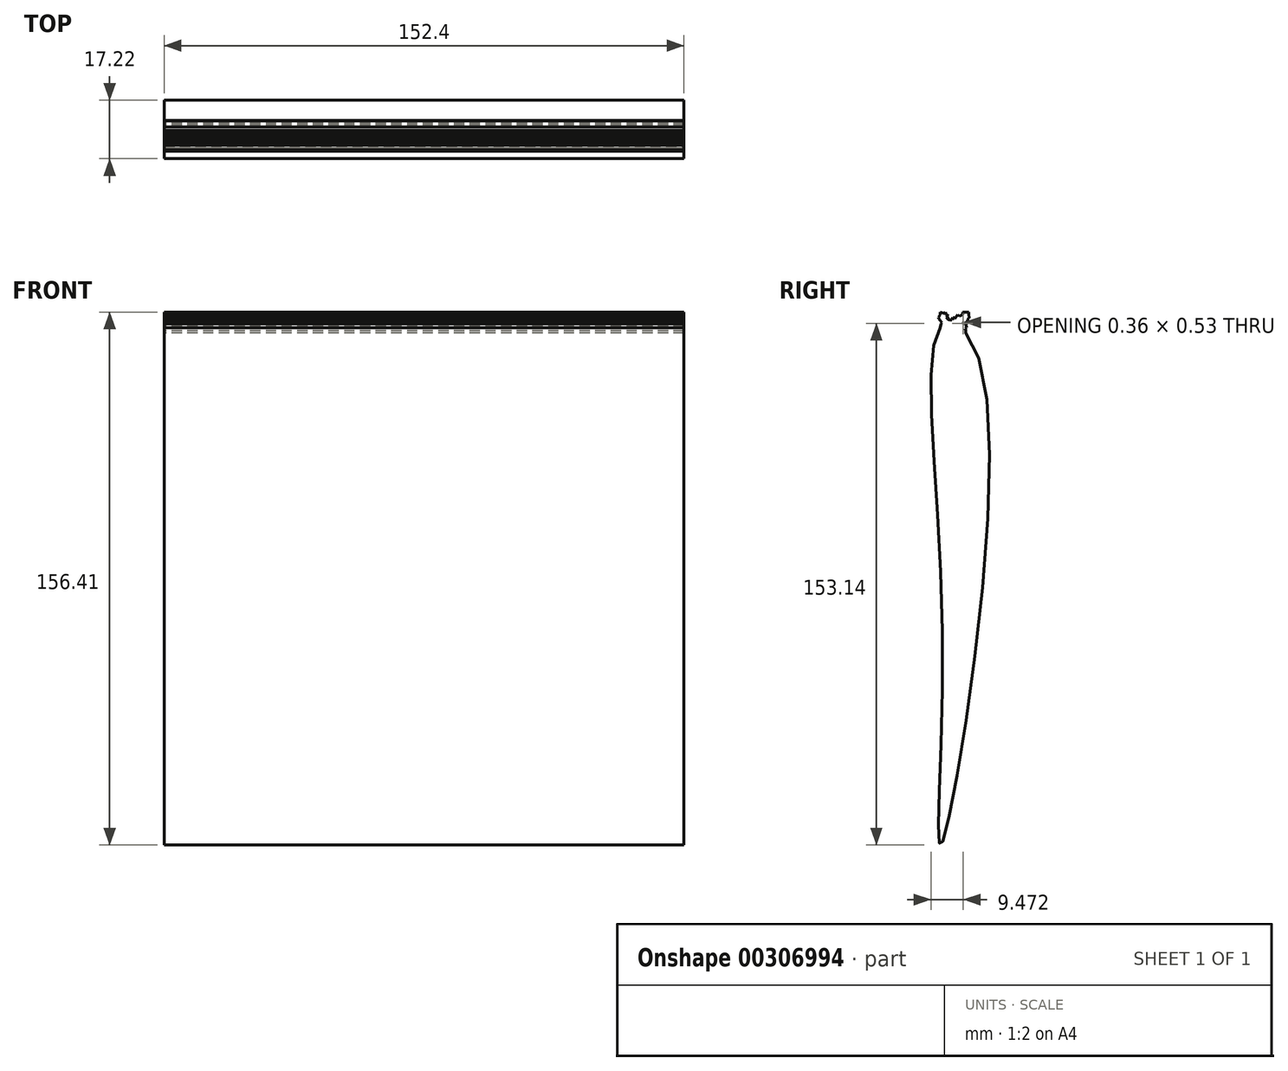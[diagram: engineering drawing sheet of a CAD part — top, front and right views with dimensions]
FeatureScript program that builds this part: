
annotation { "Feature Type Name" : "Feature", "Feature Type Description" : "" }
export const myFeature = defineFeature(function(context is Context, id is Id, definition is map)
    precondition{}
    {
        {
            var Q0;
            Q0=qCreatedBy(makeId("Right.planeOp"),FACE);
            var sketch = newSketch(context, id + "F0", { "sketchPlane" : qUnion([Q0])});
            skFitSpline(sketch, "E0", {"points": [v(-2.03, 75.34) * mm, v(9.75, 62.3) * mm, v(-2.03, -76.46) * mm, v(-2.03, -8.77) * mm, v(-2.03, 75.34) * mm]});
            skLineSegment(sketch, "E1", {"start": v(2.07, 75.7) * mm, "end": v(4.3, 78.57) * mm});
            skLineSegment(sketch, "E2", {"start": v(4.3, 78.57) * mm, "end": v(5.36, 77.85) * mm});
            skLineSegment(sketch, "E3", {"start": v(5.36, 77.85) * mm, "end": v(3.36, 74.88) * mm});
            skLineSegment(sketch, "E4", {"start": v(3.36, 74.88) * mm, "end": v(2.07, 75.7) * mm});
            skLineSegment(sketch, "E5", {"start": v(4.3, 78.57) * mm, "end": v(4.83, 79.37) * mm});
            skPoint(sketch, "E5.endSnap0", {"position": v(4.83, 78.21) * mm});
            skLineSegment(sketch, "E6", {"start": v(4.83, 79.37) * mm, "end": v(5.85, 78.57) * mm});
            skLineSegment(sketch, "E7", {"start": v(5.85, 78.57) * mm, "end": v(5.36, 77.85) * mm});
            skLineSegment(sketch, "E8", {"start": v(-0.41, 76.14) * mm, "end": v(-1.44, 78.57) * mm});
            skLineSegment(sketch, "E9", {"start": v(-1.44, 78.57) * mm, "end": v(-2.63, 78.07) * mm});
            skLineSegment(sketch, "E10", {"start": v(-2.63, 78.07) * mm, "end": v(-1.62, 75.65) * mm});
            skLineSegment(sketch, "E11", {"start": v(-1.62, 75.65) * mm, "end": v(-0.41, 76.14) * mm});
            skLineSegment(sketch, "E12", {"start": v(4, 74.4) * mm, "end": v(4, 75.84) * mm});
            skLineSegment(sketch, "E13", {"start": v(4, 75.84) * mm, "end": v(4.36, 76.36) * mm});
            skLineSegment(sketch, "E14", {"start": v(4.36, 76.36) * mm, "end": v(4.36, 76.1) * mm});
            skPoint(sketch, "E14.endSnap0", {"position": v(4.18, 76.1) * mm});
            skLineSegment(sketch, "E15", {"start": v(4.36, 76.1) * mm, "end": v(4, 75.84) * mm});
            skLineSegment(sketch, "E16", {"start": v(4, 75.12) * mm, "end": v(4.58, 75.97) * mm});
            skLineSegment(sketch, "E17", {"start": v(4.58, 75.97) * mm, "end": v(4.58, 76.68) * mm});
            skLineSegment(sketch, "E18", {"start": v(4.58, 76.68) * mm, "end": v(5.04, 76.37) * mm});
            skLineSegment(sketch, "E19", {"start": v(5.04, 76.37) * mm, "end": v(4.58, 75.97) * mm});
            skLineSegment(sketch, "E20", {"start": v(5.08, 77.44) * mm, "end": v(5.93, 77.44) * mm});
            skLineSegment(sketch, "E21", {"start": v(5.93, 77.44) * mm, "end": v(5.36, 77.85) * mm});
            skLineSegment(sketch, "E22", {"start": v(5.85, 78.57) * mm, "end": v(5.93, 77.85) * mm});
            skLineSegment(sketch, "E23", {"start": v(5.93, 77.85) * mm, "end": v(5.36, 77) * mm});
            skLineSegment(sketch, "E24", {"start": v(5.36, 77) * mm, "end": v(4.58, 76.68) * mm});
            skLineSegment(sketch, "E25", {"start": v(5.36, 77) * mm, "end": v(5.36, 76.68) * mm});
            skLineSegment(sketch, "E26", {"start": v(5.36, 76.68) * mm, "end": v(5.04, 76.37) * mm});
            skLineSegment(sketch, "E27", {"start": v(5.93, 77.85) * mm, "end": v(5.36, 77.85) * mm});
            skLineSegment(sketch, "E28", {"start": v(5.04, 76.37) * mm, "end": v(5.04, 75.4) * mm});
            skLineSegment(sketch, "E29", {"start": v(5.04, 75.4) * mm, "end": v(4, 75.12) * mm});
            skLineSegment(sketch, "E30", {"start": v(5.85, 78.57) * mm, "end": v(5.85, 79.37) * mm});
            skLineSegment(sketch, "E31", {"start": v(5.85, 79.37) * mm, "end": v(5.5, 78.84) * mm});
            skLineSegment(sketch, "E32", {"start": v(5.5, 78.84) * mm, "end": v(5.85, 79.37) * mm});
            skLineSegment(sketch, "E33", {"start": v(5.85, 79.37) * mm, "end": v(4.83, 79.37) * mm});
            skLineSegment(sketch, "E34", {"start": v(4.83, 79.37) * mm, "end": v(4, 79.37) * mm});
            skLineSegment(sketch, "E35", {"start": v(4, 79.37) * mm, "end": v(4, 78.57) * mm});
            skLineSegment(sketch, "E36", {"start": v(4, 78.57) * mm, "end": v(3.06, 78.21) * mm});
            skLineSegment(sketch, "E37", {"start": v(3.06, 78.21) * mm, "end": v(2.53, 78.57) * mm});
            skLineSegment(sketch, "E38", {"start": v(2.53, 78.57) * mm, "end": v(2.53, 77.44) * mm});
            skLineSegment(sketch, "E39", {"start": v(2.53, 77.44) * mm, "end": v(2.53, 77) * mm});
            skLineSegment(sketch, "E40", {"start": v(2.53, 77) * mm, "end": v(1.8, 76.83) * mm});
            skLineSegment(sketch, "E41", {"start": v(1.8, 76.83) * mm, "end": v(1.8, 75.93) * mm});
            skLineSegment(sketch, "E42", {"start": v(1.8, 75.93) * mm, "end": v(2.07, 75.7) * mm});
            skLineSegment(sketch, "E43", {"start": v(2.53, 78.57) * mm, "end": v(1.76, 77.44) * mm});
            skLineSegment(sketch, "E44", {"start": v(1.76, 77.44) * mm, "end": v(1.15, 77.85) * mm});
            skLineSegment(sketch, "E45", {"start": v(1.15, 77.85) * mm, "end": v(0.91, 77) * mm});
            skLineSegment(sketch, "E46", {"start": v(0.91, 77) * mm, "end": v(0.2, 77) * mm});
            skLineSegment(sketch, "E47", {"start": v(0.2, 77) * mm, "end": v(-0.25, 76.33) * mm});
            skLineSegment(sketch, "E48", {"start": v(0.2, 77) * mm, "end": v(-0.45, 77.44) * mm});
            skLineSegment(sketch, "E49", {"start": v(-0.45, 77.44) * mm, "end": v(-0.74, 77) * mm});
            skLineSegment(sketch, "E50", {"start": v(-0.74, 77) * mm, "end": v(-0.74, 77.85) * mm});
            skLineSegment(sketch, "E51", {"start": v(-0.74, 77.85) * mm, "end": v(-1.28, 78.21) * mm});
            skLineSegment(sketch, "E52", {"start": v(-1.28, 78.21) * mm, "end": v(-1.44, 78.57) * mm});
            skLineSegment(sketch, "E53", {"start": v(-0.74, 77.85) * mm, "end": v(-0.74, 78.57) * mm});
            skLineSegment(sketch, "E54", {"start": v(-0.74, 78.57) * mm, "end": v(-1.28, 78.21) * mm});
            skLineSegment(sketch, "E55", {"start": v(-0.74, 78.57) * mm, "end": v(-0.2, 78.21) * mm});
            skLineSegment(sketch, "E56", {"start": v(-0.2, 78.21) * mm, "end": v(-0.74, 77.85) * mm});
            skLineSegment(sketch, "E57", {"start": v(-0.74, 78.57) * mm, "end": v(-1.07, 79.37) * mm});
            skLineSegment(sketch, "E58", {"start": v(-1.07, 79.37) * mm, "end": v(-1.44, 78.57) * mm});
            skLineSegment(sketch, "E59", {"start": v(-1.44, 78.57) * mm, "end": v(-2.04, 78.98) * mm});
            skPoint(sketch, "E59.endSnap0", {"position": v(-2.04, 78.32) * mm});
            skLineSegment(sketch, "E60", {"start": v(-2.04, 78.98) * mm, "end": v(-2.63, 78.07) * mm});
            skLineSegment(sketch, "E61", {"start": v(-2.63, 78.07) * mm, "end": v(-2.63, 79.37) * mm});
            skLineSegment(sketch, "E62", {"start": v(-2.63, 79.37) * mm, "end": v(-1.26, 78.97) * mm});
            skLineSegment(sketch, "E63", {"start": v(-1.26, 78.97) * mm, "end": v(-1.07, 79.37) * mm});
            skLineSegment(sketch, "E64", {"start": v(-2.63, 78.57) * mm, "end": v(-3.12, 77.85) * mm});
            skLineSegment(sketch, "E65", {"start": v(-3.12, 77.85) * mm, "end": v(-2.04, 76.68) * mm});
            skLineSegment(sketch, "E66", {"start": v(-2.04, 76.68) * mm, "end": v(-2.74, 77) * mm});
            skLineSegment(sketch, "E67", {"start": v(-2.74, 77) * mm, "end": v(-2.92, 77.44) * mm});
            skLineSegment(sketch, "E68", {"start": v(-2.92, 77.44) * mm, "end": v(-3.12, 77.85) * mm});
            skLineSegment(sketch, "E69", {"start": v(-1.62, 75.65) * mm, "end": v(-2.03, 75.34) * mm});
            skLineSegment(sketch, "E70", {"start": v(-2.03, 75.34) * mm, "end": v(-2.3, 75.97) * mm});
            skLineSegment(sketch, "E71", {"start": v(-2.3, 75.97) * mm, "end": v(-1.96, 76.6) * mm});
            skLineSegment(sketch, "E72", {"start": v(-1.96, 76.6) * mm, "end": v(-2.74, 77) * mm});
            skLineSegment(sketch, "E73", {"start": v(-2.74, 77) * mm, "end": v(-2.13, 76.29) * mm});
            skLineSegment(sketch, "E74", {"start": v(5.04, 75.4) * mm, "end": v(5.22, 74.71) * mm});
            skLineSegment(sketch, "E75", {"start": v(5.22, 74.71) * mm, "end": v(4.73, 74.53) * mm});
            skLineSegment(sketch, "E76", {"start": v(4.73, 74.53) * mm, "end": v(4.95, 73.93) * mm});
            skLineSegment(sketch, "E77", {"start": v(4.95, 73.93) * mm, "end": v(4.95, 73.27) * mm});
            skLineSegment(sketch, "E78", {"start": v(4.95, 73.27) * mm, "end": v(4, 74.4) * mm});
            skLineSegment(sketch, "E79", {"start": v(-2.3, 75.97) * mm, "end": v(-2.53, 74.81) * mm});
            skLineSegment(sketch, "E80", {"start": v(-2.53, 74.81) * mm, "end": v(-2.03, 75.34) * mm});
            skLineSegment(sketch, "E81", {"start": v(-0.74, 77.85) * mm, "end": v(-0.45, 77.44) * mm});
            skSolve(sketch);
        }
        {
            var Q0;
            Q0 = qSketchRegion(id + "F0", true);
            var Q1;
            Q1=makeQuery(id+"F0.imprint","IMPRINT",FACE,{"disambiguationData":[TD([[makeQuery(id+"F0.imprint","IMPRINT",EDGE,{"derivedFrom":sQuery(id+"F0.wireOp",EDGE,"E1")}),1.0]])]});
            var Q2;
            {var subQ3=sQuery(id+"F0.wireOp",EDGE,"E1");Q2=makeQuery(id+"F0.imprint","IMPRINT",FACE,{"disambiguationData":[TD([[makeQuery(id+"F0.imprint","IMPRINT",EDGE,{"derivedFrom":subQ3}),-1.0]])]});}
            var Q3;
            {var subQ0=sQuery(id+"F0.wireOp",EDGE,"E29");Q3=makeQuery(id+"F0.imprint","IMPRINT",FACE,{"disambiguationData":[TD([[makeQuery(id+"F0.imprint","IMPRINT",EDGE,{"derivedFrom":subQ0}),1.0]])]});}
            var Q4;
            {var subQ0=sQuery(id+"F0.wireOp",EDGE,"E78");var subQ1=sQuery(id+"F0.wireOp",EDGE,"E12");var subQ2=makeQuery(id+"F0.imprint","INTERSECT",VERTEX,{"derivedFrom":[subQ1,subQ0]});Q4=makeQuery(id+"F0.imprint","IMPRINT",FACE,{"disambiguationData":[TD([[makeQuery(id+"F0.imprint","IMPRINT",EDGE,{"disambiguationData":[TD([[subQ2,1.0]])],"derivedFrom":subQ0}),1.0]])]});}
            var Q5;
            {var subQ2=sQuery(id+"F0.wireOp",EDGE,"E8");Q5=makeQuery(id+"F0.imprint","IMPRINT",FACE,{"disambiguationData":[TD([[makeQuery(id+"F0.imprint","IMPRINT",EDGE,{"derivedFrom":subQ2}),-1.0]])]});}
            var Q6;
            {var subQ0=sQuery(id+"F0.wireOp",EDGE,"E11");Q6=makeQuery(id+"F0.imprint","IMPRINT",FACE,{"disambiguationData":[TD([[makeQuery(id+"F0.imprint","IMPRINT",EDGE,{"derivedFrom":subQ0}),1.0]])]});}
            var Q7;
            {var subQ0=sQuery(id+"F0.wireOp",EDGE,"E4");Q7=makeQuery(id+"F0.imprint","IMPRINT",FACE,{"disambiguationData":[TD([[makeQuery(id+"F0.imprint","IMPRINT",EDGE,{"derivedFrom":subQ0}),-1.0]])]});}
            var Q8;
            {var subQ0=sQuery(id+"F0.wireOp",EDGE,"E78");var subQ1=sQuery(id+"F0.wireOp",EDGE,"E0");var subQ3=makeQuery(id+"F0.imprint","INTERSECT",VERTEX,{"derivedFrom":[subQ1,subQ0]});Q8=makeQuery(id+"F0.imprint","IMPRINT",FACE,{"disambiguationData":[TD([[makeQuery(id+"F0.imprint","IMPRINT",EDGE,{"disambiguationData":[TD([[subQ3,-1.0]])],"derivedFrom":subQ1}),-1.0]])]});}
            var Q9;
            {var subQ6=sQuery(id+"F0.wireOp",EDGE,"E8");Q9=makeQuery(id+"F0.imprint","IMPRINT",FACE,{"disambiguationData":[TD([[makeQuery(id+"F0.imprint","IMPRINT",EDGE,{"derivedFrom":subQ6}),1.0]])]});}
            var Q10;
            Q10=makeQuery(id+"F0.imprint","IMPRINT",FACE,{"disambiguationData":[TD([[makeQuery(id+"F0.imprint","IMPRINT",EDGE,{"derivedFrom":sQuery(id+"F0.wireOp",EDGE,"E58")}),-1.0]])]});
            var Q11;
            {var subQ0=sQuery(id+"F0.wireOp",EDGE,"E69");Q11=makeQuery(id+"F0.imprint","IMPRINT",FACE,{"disambiguationData":[TD([[makeQuery(id+"F0.imprint","IMPRINT",EDGE,{"derivedFrom":subQ0}),-1.0]])]});}
            var Q12;
            {var subQ1=sQuery(id+"F0.wireOp",EDGE,"E70");Q12=makeQuery(id+"F0.imprint","IMPRINT",FACE,{"disambiguationData":[TD([[makeQuery(id+"F0.imprint","IMPRINT",EDGE,{"derivedFrom":subQ1}),1.0]])]});}
            var Q13;
            {var subQ0=sQuery(id+"F0.wireOp",EDGE,"E80");Q13=makeQuery(id+"F0.imprint","IMPRINT",FACE,{"disambiguationData":[TD([[makeQuery(id+"F0.imprint","IMPRINT",EDGE,{"derivedFrom":subQ0}),1.0]])]});}
            var Q14;
            {var subQ5=sQuery(id+"F0.wireOp",EDGE,"E64");Q14=makeQuery(id+"F0.imprint","IMPRINT",FACE,{"disambiguationData":[TD([[makeQuery(id+"F0.imprint","IMPRINT",EDGE,{"derivedFrom":subQ5}),1.0]])]});}
            var Q15;
            {var subQ1=sQuery(id+"F0.wireOp",EDGE,"E70");Q15=makeQuery(id+"F0.imprint","IMPRINT",FACE,{"disambiguationData":[TD([[makeQuery(id+"F0.imprint","IMPRINT",EDGE,{"derivedFrom":subQ1}),-1.0]])]});}
            var Q16;
            {var subQ0=sQuery(id+"F0.wireOp",EDGE,"E67");Q16=makeQuery(id+"F0.imprint","IMPRINT",FACE,{"disambiguationData":[TD([[makeQuery(id+"F0.imprint","IMPRINT",EDGE,{"derivedFrom":subQ0}),-1.0]])]});}
            var Q17;
            {var subQ0=sQuery(id+"F0.wireOp",EDGE,"E72");var subQ1=sQuery(id+"F0.wireOp",EDGE,"E10");var subQ2=makeQuery(id+"F0.imprint","INTERSECT",VERTEX,{"derivedFrom":[subQ1,subQ0]});Q17=makeQuery(id+"F0.imprint","IMPRINT",FACE,{"disambiguationData":[TD([[makeQuery(id+"F0.imprint","IMPRINT",EDGE,{"disambiguationData":[TD([[subQ2,-1.0]])],"derivedFrom":subQ1}),1.0]])]});}
            var Q18;
            Q18=makeQuery(id+"F0.imprint","IMPRINT",FACE,{"disambiguationData":[TD([[makeQuery(id+"F0.imprint","IMPRINT",EDGE,{"derivedFrom":sQuery(id+"F0.wireOp",EDGE,"E9")}),-1.0]])]});
            var Q19;
            Q19=makeQuery(id+"F0.imprint","IMPRINT",FACE,{"disambiguationData":[TD([[makeQuery(id+"F0.imprint","IMPRINT",EDGE,{"derivedFrom":sQuery(id+"F0.wireOp",EDGE,"E17")}),-1.0]])]});
            var Q20;
            {var subQ0=sQuery(id+"F0.wireOp",EDGE,"E65");var subQ1=sQuery(id+"F0.wireOp",EDGE,"E10");var subQ2=makeQuery(id+"F0.imprint","INTERSECT",VERTEX,{"derivedFrom":[subQ1,subQ0]});Q20=makeQuery(id+"F0.imprint","IMPRINT",FACE,{"disambiguationData":[TD([[makeQuery(id+"F0.imprint","IMPRINT",EDGE,{"disambiguationData":[TD([[subQ2,-1.0]])],"derivedFrom":subQ1}),1.0]])]});}
            var Q21;
            Q21=makeQuery(id+"F0.imprint","IMPRINT",FACE,{"disambiguationData":[TD([[makeQuery(id+"F0.imprint","IMPRINT",EDGE,{"derivedFrom":sQuery(id+"F0.wireOp",EDGE,"E18")}),1.0]])]});
            var Q22;
            Q22=makeQuery(id+"F0.imprint","IMPRINT",FACE,{"disambiguationData":[TD([[makeQuery(id+"F0.imprint","IMPRINT",EDGE,{"derivedFrom":sQuery(id+"F0.wireOp",EDGE,"E49")}),-1.0]])]});
            var Q23;
            {var subQ2=sQuery(id+"F0.wireOp",EDGE,"E32");Q23=makeQuery(id+"F0.imprint","IMPRINT",FACE,{"disambiguationData":[TD([[makeQuery(id+"F0.imprint","IMPRINT",EDGE,{"derivedFrom":subQ2}),1.0]])]});}
            var Q24;
            {var subQ0=sQuery(id+"F0.wireOp",EDGE,"E66");var subQ1=sQuery(id+"F0.wireOp",EDGE,"E10");var subQ2=makeQuery(id+"F0.imprint","INTERSECT",VERTEX,{"derivedFrom":[subQ1,subQ0]});Q24=makeQuery(id+"F0.imprint","IMPRINT",FACE,{"disambiguationData":[TD([[makeQuery(id+"F0.imprint","IMPRINT",EDGE,{"disambiguationData":[TD([[subQ2,-1.0]])],"derivedFrom":subQ1}),-1.0]])]});}
            var Q25;
            Q25=makeQuery(id+"F0.imprint","IMPRINT",FACE,{"disambiguationData":[TD([[makeQuery(id+"F0.imprint","IMPRINT",EDGE,{"derivedFrom":sQuery(id+"F0.wireOp",EDGE,"E2")}),1.0]])]});
            var Q26;
            {var subQ5=sQuery(id+"F0.wireOp",EDGE,"E73");Q26=makeQuery(id+"F0.imprint","IMPRINT",FACE,{"disambiguationData":[TD([[makeQuery(id+"F0.imprint","IMPRINT",EDGE,{"derivedFrom":subQ5}),1.0]])]});}
            var Q27;
            {var subQ1=sQuery(id+"F0.wireOp",EDGE,"E14");Q27=makeQuery(id+"F0.imprint","IMPRINT",FACE,{"disambiguationData":[TD([[makeQuery(id+"F0.imprint","IMPRINT",EDGE,{"derivedFrom":subQ1}),1.0]])]});}
            var Q28;
            Q28=makeQuery(id+"F0.imprint","IMPRINT",FACE,{"disambiguationData":[TD([[makeQuery(id+"F0.imprint","IMPRINT",EDGE,{"derivedFrom":sQuery(id+"F0.wireOp",EDGE,"E16")}),-1.0]])]});
            var Q29;
            {var subQ0=sQuery(id+"F0.wireOp",EDGE,"E24");Q29=makeQuery(id+"F0.imprint","IMPRINT",FACE,{"disambiguationData":[TD([[makeQuery(id+"F0.imprint","IMPRINT",EDGE,{"derivedFrom":subQ0}),-1.0]])]});}
            var Q30;
            Q30=makeQuery(id+"F0.imprint","IMPRINT",FACE,{"disambiguationData":[TD([[makeQuery(id+"F0.imprint","IMPRINT",EDGE,{"derivedFrom":sQuery(id+"F0.wireOp",EDGE,"E13")}),-1.0]])]});
            var Q31;
            {var subQ0=sQuery(id+"F0.wireOp",EDGE,"E21");var subQ1=sQuery(id+"F0.wireOp",EDGE,"E20");var subQ2=makeQuery(id+"F0.imprint","INTERSECT",VERTEX,{"derivedFrom":[subQ1,subQ0]});Q31=makeQuery(id+"F0.imprint","IMPRINT",FACE,{"disambiguationData":[TD([[makeQuery(id+"F0.imprint","IMPRINT",EDGE,{"disambiguationData":[TD([[subQ2,1.0]])],"derivedFrom":subQ1}),1.0]])]});}
            var Q32;
            Q32=makeQuery(id+"F0.imprint","IMPRINT",FACE,{"disambiguationData":[TD([[makeQuery(id+"F0.imprint","IMPRINT",EDGE,{"derivedFrom":sQuery(id+"F0.wireOp",EDGE,"E53")}),-1.0]])]});
            var Q33;
            {var subQ0=sQuery(id+"F0.wireOp",EDGE,"E30");Q33=makeQuery(id+"F0.imprint","IMPRINT",FACE,{"disambiguationData":[TD([[makeQuery(id+"F0.imprint","IMPRINT",EDGE,{"derivedFrom":subQ0}),1.0]])]});}
            var Q34;
            Q34=makeQuery(id+"F0.imprint","IMPRINT",FACE,{"disambiguationData":[TD([[makeQuery(id+"F0.imprint","IMPRINT",EDGE,{"derivedFrom":sQuery(id+"F0.wireOp",EDGE,"E7")}),1.0]])]});
            var Q35;
            Q35=makeQuery(id+"F0.imprint","IMPRINT",FACE,{"disambiguationData":[TD([[makeQuery(id+"F0.imprint","IMPRINT",EDGE,{"derivedFrom":sQuery(id+"F0.wireOp",EDGE,"E51")}),-1.0]])]});
            var Q36;
            Q36=makeQuery(id+"F0.imprint","IMPRINT",FACE,{"disambiguationData":[TD([[makeQuery(id+"F0.imprint","IMPRINT",EDGE,{"derivedFrom":sQuery(id+"F0.wireOp",EDGE,"E52")}),-1.0]])]});
            var Q37;
            {var subQ1=sQuery(id+"F0.wireOp",EDGE,"E3");var subQ3=sQuery(id+"F0.wireOp",EDGE,"E20");var subQ4=makeQuery(id+"F0.imprint","INTERSECT",VERTEX,{"derivedFrom":[subQ1,subQ3]});Q37=makeQuery(id+"F0.imprint","IMPRINT",FACE,{"disambiguationData":[TD([[makeQuery(id+"F0.imprint","IMPRINT",EDGE,{"disambiguationData":[TD([[subQ4,-1.0]])],"derivedFrom":subQ3}),1.0]])]});}
            var Q38;
            {var subQ0=sQuery(id+"F0.wireOp",EDGE,"E27");Q38=makeQuery(id+"F0.imprint","IMPRINT",FACE,{"disambiguationData":[TD([[makeQuery(id+"F0.imprint","IMPRINT",EDGE,{"derivedFrom":subQ0}),1.0]])]});}
            var Q39;
            {var subQ4=sQuery(id+"F0.wireOp",EDGE,"E4");Q39=makeQuery(id+"F0.imprint","IMPRINT",FACE,{"disambiguationData":[TD([[makeQuery(id+"F0.imprint","IMPRINT",EDGE,{"derivedFrom":subQ4}),1.0]])]});}
            extrude(context, id + "F1", {"entities" : qUnion([Q0, Q1, Q2, Q3, Q4, Q5, Q6, Q7, Q8, Q9, Q10, Q11, Q12, Q13, Q14, Q15, Q16, Q17, Q18, Q19, Q20, Q21, Q22, Q23, Q24, Q25, Q26, Q27, Q28, Q29, Q30, Q31, Q32, Q33, Q34, Q35, Q36, Q37, Q38, Q39]), "depth" : 76.2 * mm, "hasSecondDirection" : true, "secondDirectionOppositeDirection" : true, "secondDirectionDepth" : 76.2 * mm});
        }
    });
